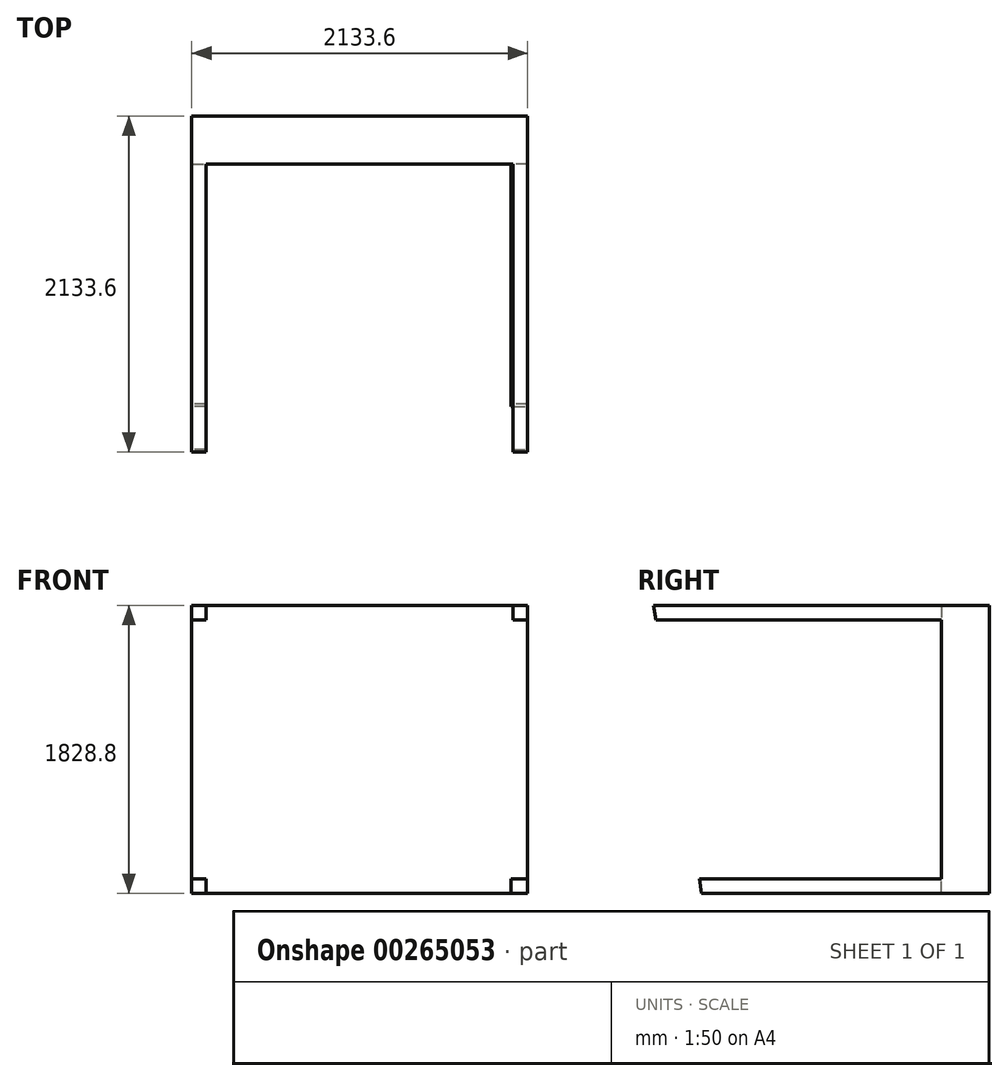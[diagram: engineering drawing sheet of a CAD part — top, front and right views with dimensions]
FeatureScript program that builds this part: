
annotation { "Feature Type Name" : "Feature", "Feature Type Description" : "" }
export const myFeature = defineFeature(function(context is Context, id is Id, definition is map)
    precondition{}
    {
        {
            var Q0;
            Q0=qCreatedBy(makeId("Front.planeOp"),FACE);
            var sketch = newSketch(context, id + "F0", { "sketchPlane" : qUnion([Q0])});
            skLineSegment(sketch, "E0.bottom", {"start": v(1066.8, -914.4) * mm, "end": v(-1066.8, -914.4) * mm});
            skLineSegment(sketch, "E0.top", {"start": v(1066.8, 914.4) * mm, "end": v(-1066.8, 914.4) * mm});
            skLineSegment(sketch, "E0.left", {"start": v(1066.8, -914.4) * mm, "end": v(1066.8, 914.4) * mm});
            skLineSegment(sketch, "E0.right", {"start": v(-1066.8, -914.4) * mm, "end": v(-1066.8, 914.4) * mm});
            skPoint(sketch, "E0.middle", {"position": v(0, 0) * mm});
            skSolve(sketch);
        }
        {
            var Q0;
            Q0 = qSketchRegion(id + "F0", true);
            extrude(context, id + "F1", {"entities" : qUnion([Q0]), "depth" : 304.8 * mm});
        }
        {
            var Q0;
            Q0=makeQuery(id+"F1.opExtrude","CAP_FACE",FACE,{"disambiguationData":[OSD([sQuery(id+"F0.wireOp",EDGE,"E0.bottom"),sQuery(id+"F0.wireOp",EDGE,"E0.top"),sQuery(id+"F0.wireOp",EDGE,"E0.left"),sQuery(id+"F0.wireOp",EDGE,"E0.right")])],"isStart":false});
            var sketch = newSketch(context, id + "F2", { "sketchPlane" : qUnion([Q0])});
            skLineSegment(sketch, "E1.bottom", {"start": v(-1066.8, 914.4) * mm, "end": v(-974.73, 914.4) * mm});
            skLineSegment(sketch, "E1.top", {"start": v(-1066.8, 822.33) * mm, "end": v(-974.73, 822.33) * mm});
            skLineSegment(sketch, "E1.left", {"start": v(-1066.8, 914.4) * mm, "end": v(-1066.8, 822.33) * mm});
            skLineSegment(sketch, "E1.right", {"start": v(-974.73, 914.4) * mm, "end": v(-974.73, 822.33) * mm});
            skLineSegment(sketch, "E2.bottom", {"start": v(1066.8, 914.4) * mm, "end": v(974.72, 914.4) * mm});
            skLineSegment(sketch, "E2.top", {"start": v(1066.8, 822.33) * mm, "end": v(974.72, 822.33) * mm});
            skLineSegment(sketch, "E2.left", {"start": v(1066.8, 914.4) * mm, "end": v(1066.8, 822.33) * mm});
            skLineSegment(sketch, "E2.right", {"start": v(974.72, 914.4) * mm, "end": v(974.72, 822.33) * mm});
            skLineSegment(sketch, "E3.bottom", {"start": v(-1066.8, -914.4) * mm, "end": v(-974.73, -914.4) * mm});
            skLineSegment(sketch, "E3.top", {"start": v(-1066.8, -822.32) * mm, "end": v(-974.73, -822.32) * mm});
            skLineSegment(sketch, "E3.left", {"start": v(-1066.8, -914.4) * mm, "end": v(-1066.8, -822.32) * mm});
            skLineSegment(sketch, "E3.right", {"start": v(-974.73, -914.4) * mm, "end": v(-974.73, -822.32) * mm});
            skLineSegment(sketch, "E4.bottom", {"start": v(1066.8, -914.4) * mm, "end": v(960.4, -914.4) * mm});
            skLineSegment(sketch, "E4.top", {"start": v(1066.8, -822.32) * mm, "end": v(960.4, -822.32) * mm});
            skLineSegment(sketch, "E4.left", {"start": v(1066.8, -914.4) * mm, "end": v(1066.8, -822.32) * mm});
            skLineSegment(sketch, "E4.right", {"start": v(960.4, -914.4) * mm, "end": v(960.4, -822.32) * mm});
            skSolve(sketch);
        }
        {
            var Q0;
            Q0=makeQuery(id+"F2.imprint","IMPRINT",FACE,{"disambiguationData":[TD([[makeQuery(id+"F2.imprint","IMPRINT",EDGE,{"derivedFrom":sQuery(id+"F2.wireOp",EDGE,"E1.bottom")}),1.0]])]});
            var Q1;
            Q1=makeQuery(id+"F2.imprint","IMPRINT",FACE,{"disambiguationData":[TD([[makeQuery(id+"F2.imprint","IMPRINT",EDGE,{"derivedFrom":sQuery(id+"F2.wireOp",EDGE,"E3.bottom")}),-1.0]])]});
            var Q2;
            Q2=makeQuery(id+"F2.imprint","IMPRINT",FACE,{"disambiguationData":[TD([[makeQuery(id+"F2.imprint","IMPRINT",EDGE,{"derivedFrom":sQuery(id+"F2.wireOp",EDGE,"E2.bottom")}),1.0]])]});
            var Q3;
            Q3=makeQuery(id+"F2.imprint","IMPRINT",FACE,{"disambiguationData":[TD([[makeQuery(id+"F2.imprint","IMPRINT",EDGE,{"derivedFrom":sQuery(id+"F2.wireOp",EDGE,"E4.bottom")}),-1.0]])]});
            extrude(context, id + "F3", {"entities" : qUnion([Q0, Q1, Q2, Q3]), "operationType" : NewBodyOperationType.ADD, "depth" : 1828.8 * mm});
        }
        {
            var Q0;
            Q0=makeQuery(id+"F3.boolean.opBoolean","MERGE",FACE,{"derivedFrom":[makeQuery(id+"F1.opExtrude","SWEPT_FACE",FACE,{"disambiguationData":[OSD([sQuery(id+"F0.wireOp",EDGE,"E0.right")])]}),makeQuery(id+"F3.opExtrude","SWEPT_FACE",FACE,{"disambiguationData":[OSD([sQuery(id+"F2.wireOp",EDGE,"E1.left")])]}),makeQuery(id+"F3.opExtrude","SWEPT_FACE",FACE,{"disambiguationData":[OSD([sQuery(id+"F2.wireOp",EDGE,"E3.left")])]})]});
            var sketch = newSketch(context, id + "F4", { "sketchPlane" : qUnion([Q0])});
            skLineSegment(sketch, "E5", {"start": v(2133.6, 914.4) * mm, "end": v(1828.8, -914.4) * mm});
            skLineSegment(sketch, "E6", {"start": v(1828.8, -914.4) * mm, "end": v(2133.6, -914.4) * mm});
            skLineSegment(sketch, "E7", {"start": v(2133.6, -914.4) * mm, "end": v(2133.6, 914.4) * mm});
            skSolve(sketch);
        }
        {
            var Q0;
            Q0 = qSketchRegion(id + "F4", true);
            extrude(context, id + "F5", {"entities" : qUnion([Q0]), "operationType" : NewBodyOperationType.REMOVE, "oppositeDirection" : true, "depth" : 2133.6 * mm});
        }
    });
